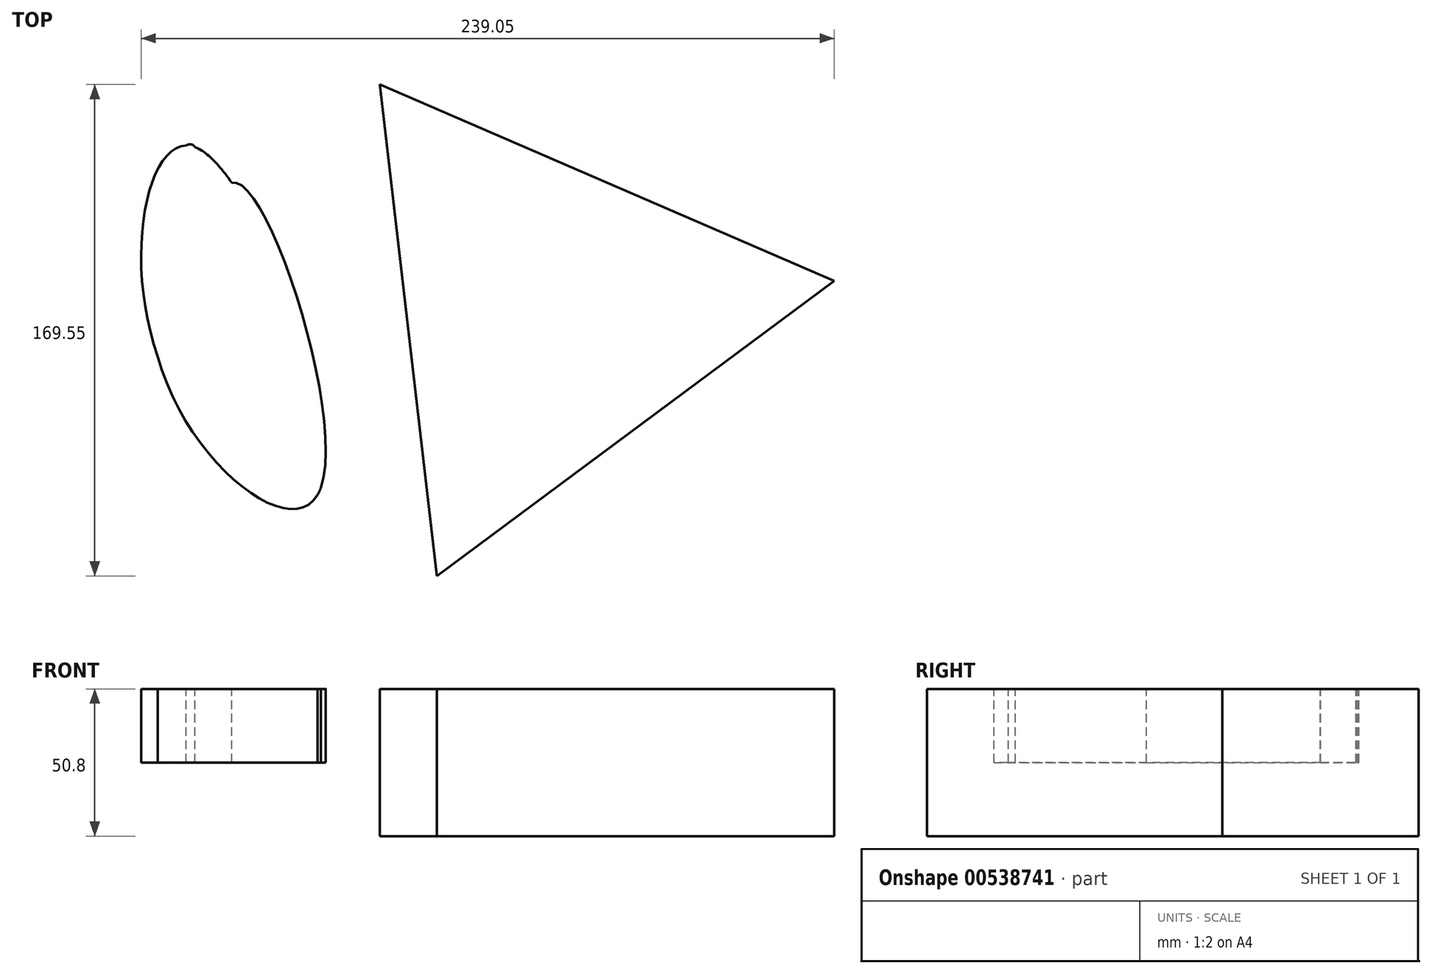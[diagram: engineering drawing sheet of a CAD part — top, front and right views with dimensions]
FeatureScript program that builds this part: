
annotation { "Feature Type Name" : "Feature", "Feature Type Description" : "" }
export const myFeature = defineFeature(function(context is Context, id is Id, definition is map)
    precondition{}
    {
        {
            var Q0;
            Q0=qCreatedBy(makeId("Top.planeOp"),FACE);
            var sketch = newSketch(context, id + "F0", { "sketchPlane" : qUnion([Q0])});
            skCircle(sketch, "E0.cCircle", {"center": v(0.98, 0.08) * mm, "radius": 49.28 * mm, "construction": true});
            skLineSegment(sketch, "E0.0", {"start": v(98.87, 11.44) * mm, "end": v(-38.12, -90.38) * mm});
            skLineSegment(sketch, "E0.1", {"start": v(-38.12, -90.38) * mm, "end": v(-57.8, 79.17) * mm});
            skLineSegment(sketch, "E0.2", {"start": v(-57.8, 79.17) * mm, "end": v(98.87, 11.44) * mm});
            skPoint(sketch, "E0.0.midPoint", {"position": v(30.37, -39.47) * mm});
            skFitSpline(sketch, "E1", {"points": [v(-134.39, -14.7) * mm, v(-121.6, 57.56) * mm, v(-79.28, -62.34) * mm, v(-134.39, -14.7) * mm]});
            skFitSpline(sketch, "E2", {"points": [v(-118.67, 12.45) * mm, v(-108.93, 45.3) * mm, v(-79.28, -62.34) * mm, v(-134.39, -14.7) * mm, v(-121.6, 57.56) * mm, v(-118.67, 12.45) * mm]});
            skSolve(sketch);
        }
        {
            var Q0;
            Q0 = qSketchRegion(id + "F0", true);
            extrude(context, id + "F1", {"entities" : qUnion([Q0]), "oppositeDirection" : true, "depth" : 25.4 * mm, "offsetDistance" : 25.4 * mm});
        }
        {
            var Q0;
            Q0=makeQuery(id+"F1.opExtrude","CAP_FACE",FACE,{"disambiguationData":[OSD([sQuery(id+"F0.wireOp",EDGE,"E0.0"),sQuery(id+"F0.wireOp",EDGE,"E0.1"),sQuery(id+"F0.wireOp",EDGE,"E0.2")])],"isStart":false});
            extrude(context, id + "F2", {"entities" : qUnion([Q0]), "operationType" : NewBodyOperationType.ADD, "depth" : 25.4 * mm, "offsetDistance" : 25.4 * mm});
        }
    });
